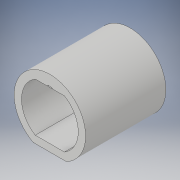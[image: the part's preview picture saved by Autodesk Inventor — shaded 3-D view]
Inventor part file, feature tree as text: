
AUTODESK INVENTOR PART (.ipt)
format: ipt  version: 2017 (Build 210142000, 142)  size: 143,872 bytes
history: native  units: in
note: dims shown in document units (in); Inventor stores cm internally (conversion verified against a paired STEP export)
features: sketch x2, other x1, extrude x1
ambient origin geometry x8: Origin, YZ Plane, XZ Plane, XY Plane, X Axis, Y Axis, Z Axis, Center Point
bodies: Solid1 (feature_tree), Solid2 (feature_tree)
feature tree (4):
  other  "corridor"
  extrude  "light"  Depth=1.0in TaperAngle=0.0deg
  sketch  "Sketch1"  dims[d0=6.6667in d1=4.0in d2=1.0in d3=11.0in d4=0.0in]
  sketch  "Sketch5"  dims[d7=1.0in d20=1.0in d21=4.8944in d23=0.5833in d26=0.125in d27=3.8873in d28=3.8873in d30=1.7083in d31=0.25in d32=0.125in d34=45.0deg d35=0.0892in d36=0.0884in d37=1.0in d38=0.0in d39=0.0625in d40=0.0625in d41=1.6458in d44=0.125in]
